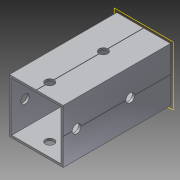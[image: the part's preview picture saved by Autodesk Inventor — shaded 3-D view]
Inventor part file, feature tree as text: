
AUTODESK INVENTOR PART (.ipt)
format: ipt  version: 2014 SP1 (Build 180222100, 222)  size: 1,193,472 bytes
history: native  units: in
note: dims shown in document units (in); Inventor stores cm internally (conversion verified against a paired STEP export)
features: extrude x2, sketch x2, pattern_circular x1, other x1, plane x1, imported_body x1
ambient origin geometry x8: Origin, YZ Plane, XZ Plane, XY Plane, X Axis, Y Axis, Z Axis, Center Point
bodies: Body1 (feature_tree)
feature tree (8):
  pattern_circular  "CirPattern2"
  other  "217-3426-STEP1"
  plane  "Work Plane1"
  extrude  "Extrusion1"  Depth=3937.0079in TaperAngle=0.0deg
  extrude  "Extrusion2"  [1 undecoded]
  imported_body  "Base1"
  sketch  "Sketch1"  dims[d0=-2.25in d1=3937.0079in d2=0.0in]
  sketch  "Sketch3"  dims[d3=0.25in d4=0.0in]
note: 1 required parameter value undecoded (feature->parameter linkage not recoverable at this tier; creation-order binding heuristic only, values carry confidence <= 0.55)
